# Revit family: RBA4605-068-RH
name_source: partatom
category: Plumbing Fixtures
units: mm (PartAtom-declared; Revit-internal decimal feet)

## family parameters
Always vertical = Yes
Cut with Voids When Loaded = No
Part Type = Normal
Room Calculation Point = No
Round Connector Dimension = Use Diameter
Shared = No
Work Plane-Based = No

## types (3) — shared parameters
CW Connection = Yes
Distance Away from Toilet (default) = 1090 mm  [stored 3.57612 ft]
Distance Away from Wall (default) = 100 mm  [stored 0.328084 ft]
HW Connection = Yes
Manufacturer = RBA Group
OFFSET = 1000 mm  [stored 3.28084 ft]
Vent Connection = Yes
Waste Connection = Yes
zero-valued in all types: Default Elevation

## per-type parameters (varying)
| type | Description | Materials and Finishes | Modified Issue | URL |
| RBA4601-061 | Raffaello Shower T-Rail | Stainless Steel / White Antibacterial Finish | 20180813.01 | http://www.rba.com.au |
| RBA4605-068-RH | Raffaello Shower T-Rail, 4 Star Shower & Mixer Set, RH | Stainless Steel / Matte Black Antibacterial Finish | 20200519.01 | www.rba.com.au |
| RBA4601-069 | Raffaello Shower T-Rail | Stainless Steel / Chrome Finish | 20180813.01 | http://www.rba.com.au |

note: column(s) folded — value = type name in every type: Model

note: [stored X ft] marks values corroborated as IEEE doubles in the binary element streams (Revit-internal decimal feet)

## geometry (parser evidence)
native form markers: Blend x4, Sweep x14
no freeform markers — native parametric forms only
